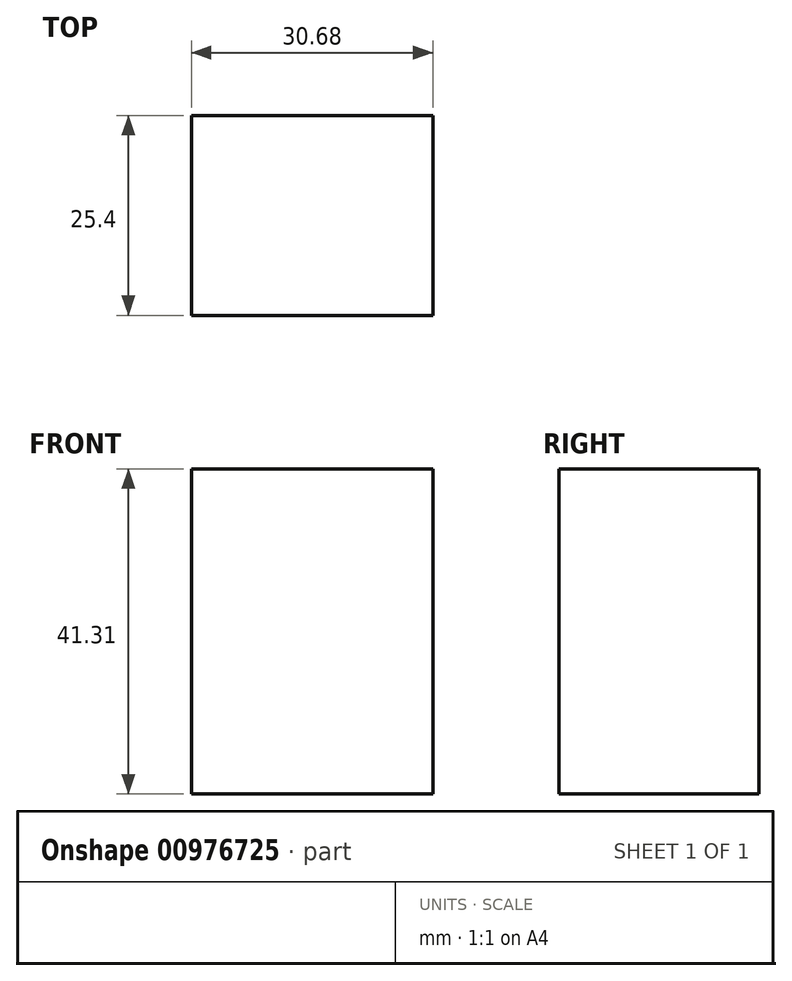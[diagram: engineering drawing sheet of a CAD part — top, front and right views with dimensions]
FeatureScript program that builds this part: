
annotation { "Feature Type Name" : "Feature", "Feature Type Description" : "" }
export const myFeature = defineFeature(function(context is Context, id is Id, definition is map)
    precondition{}
    {
        {
            var Q0;
            Q0=qCreatedBy(makeId("Front.planeOp"),FACE);
            var sketch = newSketch(context, id + "F0", { "sketchPlane" : qUnion([Q0])});
            skLineSegment(sketch, "E0.bottom", {"start": v(0, 0) * mm, "end": v(30.68, 0) * mm});
            skLineSegment(sketch, "E0.top", {"start": v(0, -41.31) * mm, "end": v(30.68, -41.31) * mm});
            skLineSegment(sketch, "E0.left", {"start": v(0, 0) * mm, "end": v(0, -41.31) * mm});
            skLineSegment(sketch, "E0.right", {"start": v(30.68, 0) * mm, "end": v(30.68, -41.31) * mm});
            skSolve(sketch);
        }
        {
            var Q0;
            Q0 = qSketchRegion(id + "F0", true);
            extrude(context, id + "F1", {"entities" : qUnion([Q0]), "depth" : 25.4 * mm, "offsetDistance" : 25.4 * mm});
        }
    });
